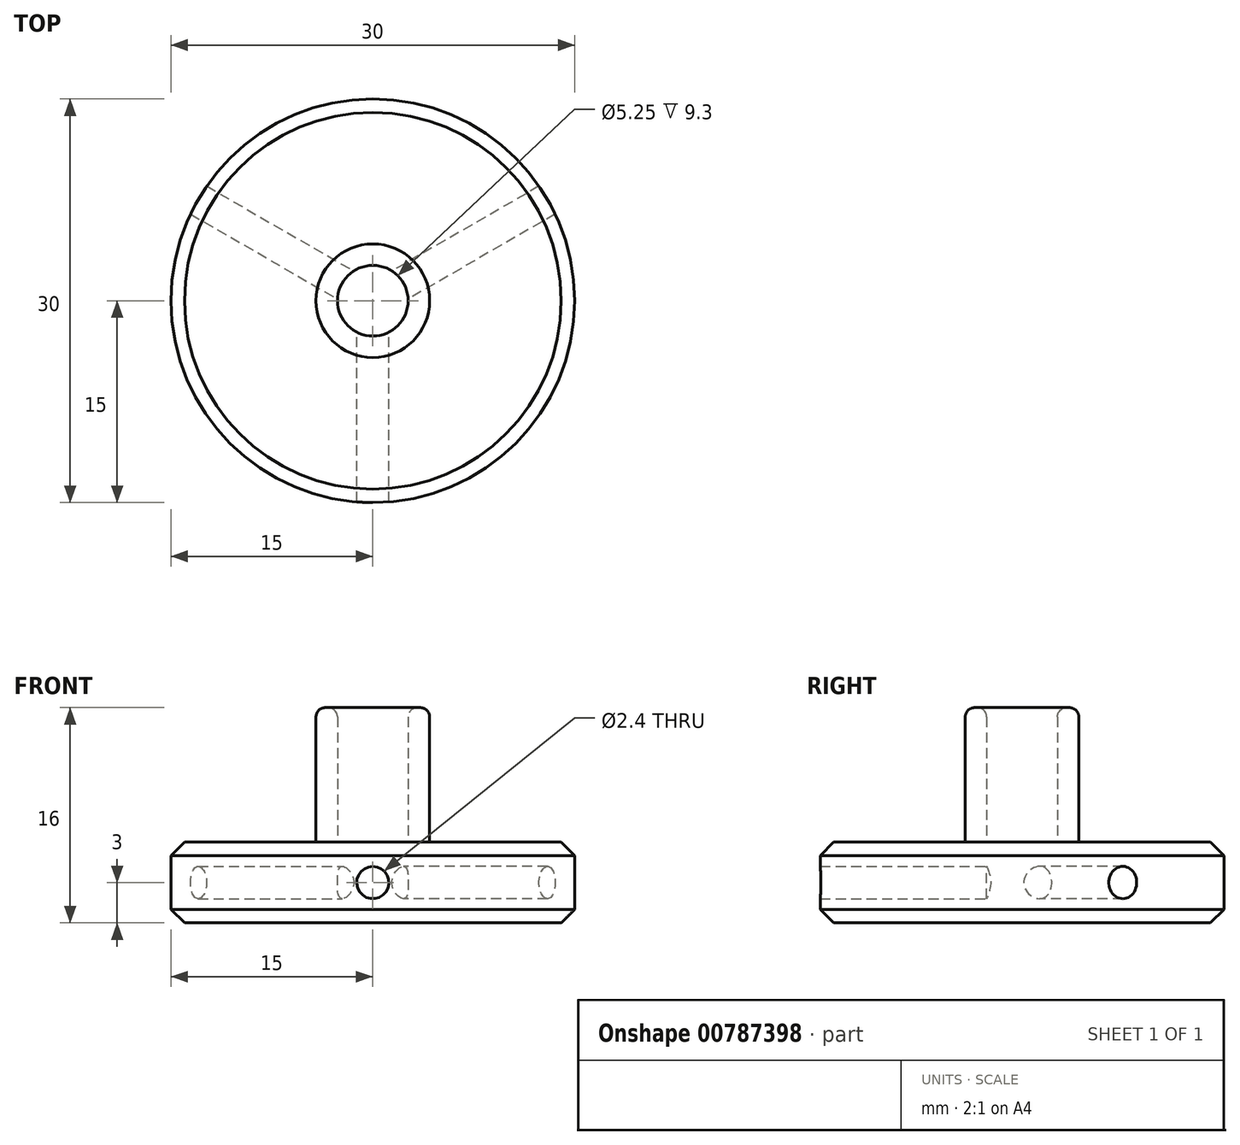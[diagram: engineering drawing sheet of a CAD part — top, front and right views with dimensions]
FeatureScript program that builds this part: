
annotation { "Feature Type Name" : "Feature", "Feature Type Description" : "" }
export const myFeature = defineFeature(function(context is Context, id is Id, definition is map)
    precondition{}
    {
        {
            var Q0;
            Q0=qCreatedBy(makeId("Top.planeOp"),FACE);
            var sketch = newSketch(context, id + "F0", { "sketchPlane" : qUnion([Q0])});
            skCircle(sketch, "E0", {"center": v(0, 0) * mm, "radius": 15 * mm});
            skLineSegment(sketch, "E1", {"start": v(0, 0) * mm, "end": v(-15, 0) * mm});
            skLineSegment(sketch, "E2", {"start": v(0, 0) * mm, "end": v(7.5, -13) * mm});
            skLineSegment(sketch, "E3.MirrorCS", {"start": v(0, 0) * mm, "end": v(7.5, 13) * mm});
            skSolve(sketch);
        }
        {
            var Q0;
            Q0=qCreatedBy(makeId("Front.planeOp"),FACE);
            var sketch = newSketch(context, id + "F1", { "sketchPlane" : qUnion([Q0])});
            skCircle(sketch, "E4", {"center": v(0, 0) * mm, "radius": 1.2 * mm});
            skLineSegment(sketch, "E5", {"start": v(0, 0) * mm, "end": v(0, 32.54) * mm});
            skSolve(sketch);
        }
        {
            var Q0;
            Q0=makeQuery(id+"F1.imprint","IMPRINT",FACE,{"disambiguationData":[TD([[makeQuery(id+"F1.imprint","IMPRINT",EDGE,{"derivedFrom":sQuery(id+"F1.wireOp",EDGE,"E4")}),1.0]])]});
            extrude(context, id + "F2", {"entities" : qUnion([Q0]), "depth" : 25 * mm, "offsetDistance" : 25 * mm});
        }
        {
            var Q0;
            Q0=makeQuery(id+"F2.opExtrude","SWEPT_BODY",BODY,{"disambiguationData":[OSD([sQuery(id+"F1.wireOp",EDGE,"E4")])]});
            var Q1;
            Q1=sQuery(id+"F1.wireOp",EDGE,"E5");
            circularPattern(context, id + "F3", {"operationType" : NewBodyOperationType.ADD, "entities" : qUnion([Q0]), "axis" : qUnion([Q1]), "angle" : 360 * degree, "instanceCount" : 3, "equalSpace" : true});
        }
        {
            var Q0;
            {var subQ0=sQuery(id+"F0.wireOp",EDGE,"E1");Q0=makeQuery(id+"F0.imprint","IMPRINT",FACE,{"disambiguationData":[TD([[makeQuery(id+"F0.imprint","IMPRINT",EDGE,{"derivedFrom":subQ0}),-1.0]])]});}
            var Q1;
            {var subQ0=sQuery(id+"F0.wireOp",EDGE,"E1");Q1=makeQuery(id+"F0.imprint","IMPRINT",FACE,{"disambiguationData":[TD([[makeQuery(id+"F0.imprint","IMPRINT",EDGE,{"derivedFrom":subQ0}),1.0]])]});}
            var Q2;
            {var subQ0=sQuery(id+"F0.wireOp",EDGE,"E2");Q2=makeQuery(id+"F0.imprint","IMPRINT",FACE,{"disambiguationData":[TD([[makeQuery(id+"F0.imprint","IMPRINT",EDGE,{"derivedFrom":subQ0}),1.0]])]});}
            var Q3;
            {var subQ0=sQuery(id+"F0.wireOp",EDGE,"E3.MirrorCS");var subQ1=sQuery(id+"F0.wireOp",EDGE,"E0");var subQ2=makeQuery(id+"F0.imprint","INTERSECT",VERTEX,{"derivedFrom":[subQ1,subQ0]});Q3=makeQuery(id+"F0.imprint","IMPRINT",FACE,{"disambiguationData":[TD([[makeQuery(id+"F0.imprint","IMPRINT",EDGE,{"disambiguationData":[TD([[subQ2,-1.0]])],"derivedFrom":subQ1}),1.0]])]});}
            var Q4;
            {var subQ0=sQuery(id+"F0.wireOp",EDGE,"E2");var subQ1=sQuery(id+"F0.wireOp",EDGE,"E0");var subQ2=makeQuery(id+"F0.imprint","INTERSECT",VERTEX,{"derivedFrom":[subQ1,subQ0]});Q4=makeQuery(id+"F0.imprint","IMPRINT",FACE,{"disambiguationData":[TD([[makeQuery(id+"F0.imprint","IMPRINT",EDGE,{"disambiguationData":[TD([[subQ2,1.0]])],"derivedFrom":subQ1}),1.0]])]});}
            var Q5;
            {var subQ0=sQuery(id+"F0.wireOp",EDGE,"E2");var subQ1=sQuery(id+"F0.wireOp",EDGE,"E0");var subQ2=makeQuery(id+"F0.imprint","INTERSECT",VERTEX,{"derivedFrom":[subQ1,subQ0]});Q5=makeQuery(id+"F0.imprint","IMPRINT",FACE,{"disambiguationData":[TD([[makeQuery(id+"F0.imprint","IMPRINT",EDGE,{"disambiguationData":[TD([[subQ2,-1.0]])],"derivedFrom":subQ1}),1.0]])]});}
            extrude(context, id + "F4", {"entities" : qUnion([Q0, Q1, Q2, Q3, Q4, Q5]), "endBound" : BoundingType.SYMMETRIC, "depth" : 6 * mm, "offsetDistance" : 25 * mm});
        }
        {
            var Q0;
            Q0=makeQuery(id+"F2.opExtrude","SWEPT_BODY",BODY,{"disambiguationData":[OSD([sQuery(id+"F1.wireOp",EDGE,"E4")])]});
            var Q1;
            Q1=makeQuery(id+"F4.opExtrude","SWEPT_BODY",BODY,{"disambiguationData":[OSD([sQuery(id+"F0.wireOp",EDGE,"E0")])]});
            booleanBodies(context, id + "F5", {"operationType" : BooleanOperationType.SUBTRACTION, "tools" : qUnion([Q0]), "targets" : qUnion([Q1])});
        }
        {
            var Q0;
            Q0=makeQuery(id+"F4.opExtrude","CAP_FACE",FACE,{"disambiguationData":[OSD([sQuery(id+"F0.wireOp",EDGE,"E0")])],"isStart":false});
            var sketch = newSketch(context, id + "F6", { "sketchPlane" : qUnion([Q0])});
            skCircle(sketch, "E6", {"center": v(0, 0) * mm, "radius": 4.22 * mm});
            skCircle(sketch, "E7", {"center": v(0, 0) * mm, "radius": 2.62 * mm});
            skSolve(sketch);
        }
        {
            var Q0;
            Q0=makeQuery(id+"F6.imprint","IMPRINT",FACE,{"disambiguationData":[TD([[makeQuery(id+"F6.imprint","IMPRINT",EDGE,{"derivedFrom":sQuery(id+"F6.wireOp",EDGE,"E6")}),1.0]])]});
            extrude(context, id + "F7", {"entities" : qUnion([Q0]), "operationType" : NewBodyOperationType.ADD, "depth" : 10 * mm, "offsetDistance" : 25 * mm});
        }
        {
            var Q0;
            Q0=makeQuery(id+"F4.opExtrude","CAP_EDGE",EDGE,{"disambiguationData":[OSD([sQuery(id+"F0.wireOp",EDGE,"E0")])],"isStart":false});
            var Q1;
            Q1=makeQuery(id+"F4.opExtrude","CAP_EDGE",EDGE,{"disambiguationData":[OSD([sQuery(id+"F0.wireOp",EDGE,"E0")])],"isStart":true});
            chamfer(context, id + "F8", {"entities" : qUnion([Q0, Q1]), "width" : 1 * mm, "tangentPropagation" : true});
        }
        {
            var Q0;
            Q0=makeQuery(id+"F7.boolean.opBoolean","SPLIT",FACE,{"disambiguationData":[TD([makeQuery(id+"F7.opExtrude","SWEPT_FACE",FACE,{"disambiguationData":[OSD([sQuery(id+"F6.wireOp",EDGE,"E7")])]})])],"derivedFrom":makeQuery(id+"F4.opExtrude","CAP_FACE",FACE,{"disambiguationData":[OSD([sQuery(id+"F0.wireOp",EDGE,"E0")])],"isStart":false})});
            extrude(context, id + "F9", {"entities" : qUnion([Q0]), "operationType" : NewBodyOperationType.ADD, "oppositeDirection" : true, "depth" : 6 * mm, "offsetDistance" : 25 * mm});
        }
        {
            var Q0;
            Q0=makeQuery(id+"F7.opExtrude","CAP_EDGE",EDGE,{"disambiguationData":[OSD([sQuery(id+"F6.wireOp",EDGE,"E7")])],"isStart":false});
            var Q1;
            Q1=makeQuery(id+"F7.opExtrude","CAP_EDGE",EDGE,{"disambiguationData":[OSD([sQuery(id+"F6.wireOp",EDGE,"E6")])],"isStart":false});
            fillet(context, id + "F10", {"entities" : qUnion([Q0, Q1]), "radius" : 0.7 * mm, "tangentPropagation" : true, "allowEdgeOverflow" : false});
        }
    });
